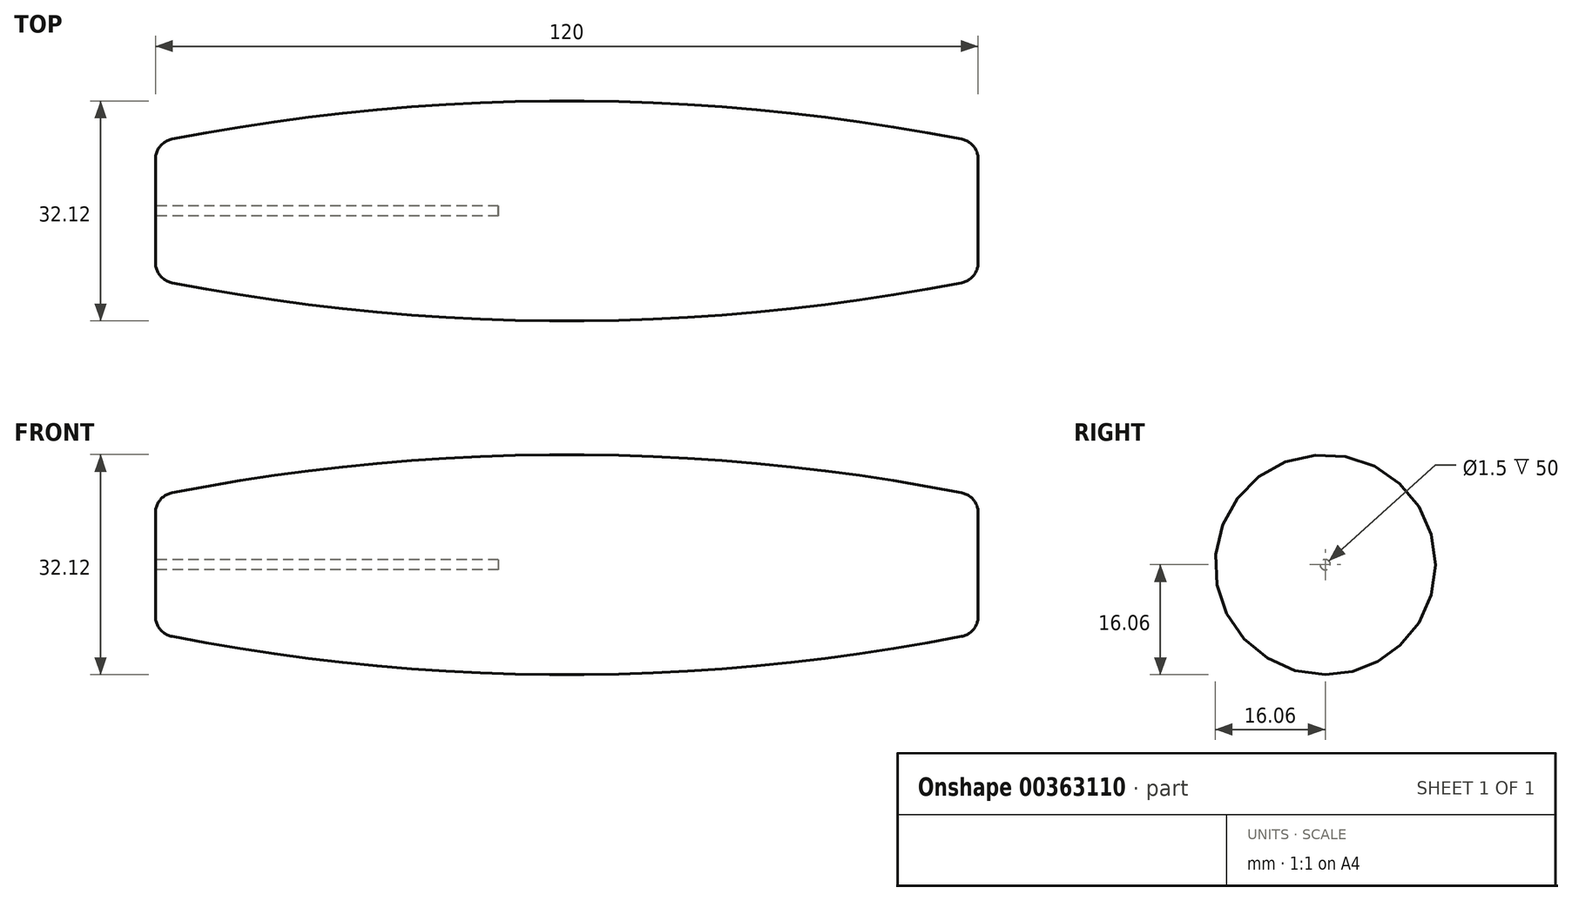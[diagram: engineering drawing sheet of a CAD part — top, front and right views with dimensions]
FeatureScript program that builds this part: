
annotation { "Feature Type Name" : "Feature", "Feature Type Description" : "" }
export const myFeature = defineFeature(function(context is Context, id is Id, definition is map)
    precondition{}
    {
        {
            var Q0;
            Q0=qCreatedBy(makeId("Top.planeOp"),FACE);
            var sketch = newSketch(context, id + "F0", { "sketchPlane" : qUnion([Q0])});
            skArc(sketch, "E0", {"start": v(60, 10) * mm, "mid": v(0, 16.06) * mm, "end": v(-60, 10) * mm});
            skLineSegment(sketch, "E1", {"start": v(-60, 0) * mm, "end": v(60, 0) * mm});
            skLineSegment(sketch, "E2", {"start": v(60, 10) * mm, "end": v(60, 0) * mm});
            skLineSegment(sketch, "E3", {"start": v(-60, 10) * mm, "end": v(-60, 0) * mm});
            skSolve(sketch);
        }
        {
            var Q0;
            Q0=makeQuery(id+"F0.imprint","IMPRINT",FACE,{"disambiguationData":[TD([[makeQuery(id+"F0.imprint","IMPRINT",EDGE,{"derivedFrom":sQuery(id+"F0.wireOp",EDGE,"E0")}),1.0]])]});
            var Q1;
            Q1=sQuery(id+"F0.wireOp",EDGE,"E1");
            revolve(context, id + "F1", {"entities" : qUnion([Q0]), "axis" : qUnion([Q1]), "revolveType" : RevolveType.FULL});
        }
        {
            var Q0;
            Q0=makeQuery(id+"F1.opRevolve","SWEPT_FACE",FACE,{"disambiguationData":[OSD([sQuery(id+"F0.wireOp",EDGE,"E3")])]});
            var sketch = newSketch(context, id + "F2", { "sketchPlane" : qUnion([Q0])});
            skCircle(sketch, "E4", {"center": v(0, 0) * mm, "radius": 0.75 * mm});
            skSolve(sketch);
        }
        {
            var Q0;
            Q0=makeQuery(id+"F2.imprint","IMPRINT",FACE,{"disambiguationData":[TD([[makeQuery(id+"F2.imprint","IMPRINT",EDGE,{"derivedFrom":sQuery(id+"F2.wireOp",EDGE,"E4")}),1.0]])]});
            extrude(context, id + "F3", {"entities" : qUnion([Q0]), "operationType" : NewBodyOperationType.REMOVE, "oppositeDirection" : true, "depth" : 50 * mm});
        }
        {
            var Q0;
            Q0=makeQuery(id+"F1.opRevolve","SWEPT_EDGE",EDGE,{"disambiguationData":[OSD([sQuery(id+"F0.wireOp",EDGE,"E0"),sQuery(id+"F0.wireOp",EDGE,"E3")])]});
            var Q1;
            Q1=makeQuery(id+"F1.opRevolve","SWEPT_EDGE",EDGE,{"disambiguationData":[OSD([sQuery(id+"F0.wireOp",EDGE,"E0"),sQuery(id+"F0.wireOp",EDGE,"E2")])]});
            fillet(context, id + "F4", {"entities" : qUnion([Q0, Q1]), "radius" : 3 * mm, "tangentPropagation" : true, "allowEdgeOverflow" : false});
        }
    });
